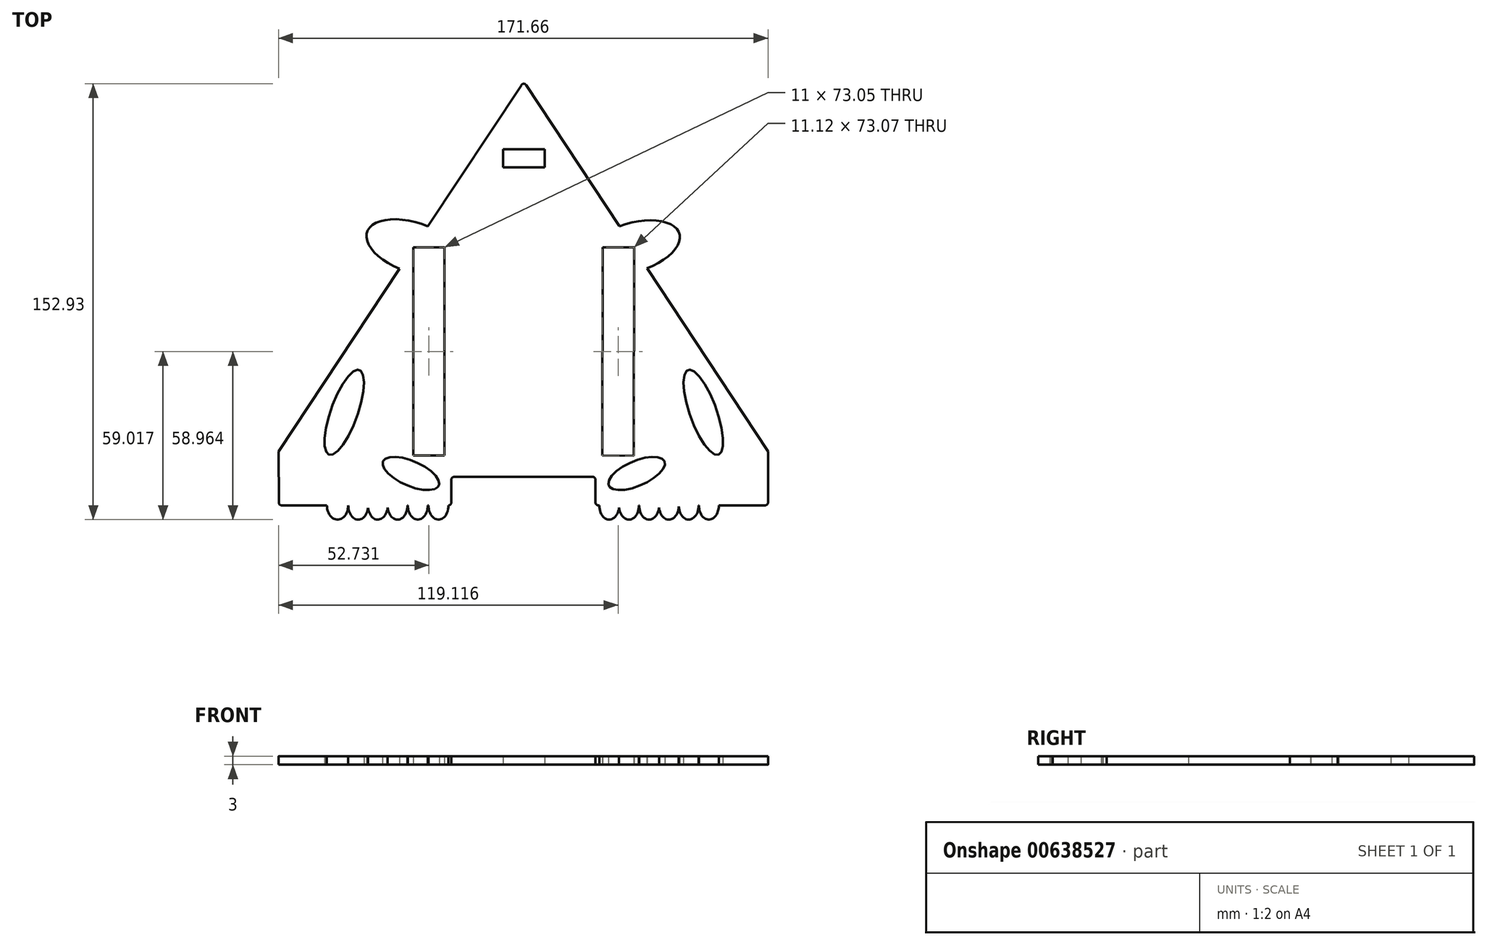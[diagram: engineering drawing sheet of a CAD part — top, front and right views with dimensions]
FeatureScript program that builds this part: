
annotation { "Feature Type Name" : "Feature", "Feature Type Description" : "" }
export const myFeature = defineFeature(function(context is Context, id is Id, definition is map)
    precondition{}
    {
        {
            var Q0;
            Q0=qCreatedBy(makeId("Top.planeOp"),FACE);
            var sketch = newSketch(context, id + "F0", { "sketchPlane" : qUnion([Q0])});
            skPoint(sketch, "E0.0.midPoint", {"position": v(0, -49.5) * mm});
            skPoint(sketch, "E0.cCircle.center.orphan", {"position": v(0, 0) * mm});
            skLineSegment(sketch, "E1", {"start": v(-84.79, -49.5) * mm, "end": v(-54.5, -49.5) * mm});
            skLineSegment(sketch, "E2", {"start": v(84.78, -49.5) * mm, "end": v(26.28, -49.5) * mm});
            skLineSegment(sketch, "E3", {"start": v(25.28, -48.5) * mm, "end": v(25.28, -40.5) * mm});
            skLineSegment(sketch, "E4", {"start": v(24.28, -39.5) * mm, "end": v(-24.28, -39.5) * mm});
            skLineSegment(sketch, "E5", {"start": v(-25.28, -40.5) * mm, "end": v(-25.28, -48.5) * mm});
            skPoint(sketch, "E6.visualSharp", {"position": v(0.12, 99.24) * mm});
            skLineSegment(sketch, "E7", {"start": v(0.95, 97.98) * mm, "end": v(33.62, 48.48) * mm});
            skLineSegment(sketch, "E8", {"start": v(85.78, -30.56) * mm, "end": v(85.78, -48.5) * mm});
            skLineSegment(sketch, "E9", {"start": v(-85.88, -30.62) * mm, "end": v(-85.79, -48.5) * mm});
            skLineSegment(sketch, "E10", {"start": v(-0.72, 97.98) * mm, "end": v(-33.51, 48.46) * mm});
            skArc(sketch, "E11.filletArc", {"start": v(0.95, 97.98) * mm, "mid": v(0.12, 98.43) * mm, "end": v(-0.72, 97.98) * mm});
            skPoint(sketch, "E12.visualSharp", {"position": v(85.78, -49.5) * mm});
            skArc(sketch, "E12.filletArc", {"start": v(84.78, -49.5) * mm, "mid": v(85.49, -49.2) * mm, "end": v(85.78, -48.5) * mm});
            skPoint(sketch, "E13.visualSharp", {"position": v(25.28, -49.5) * mm});
            skArc(sketch, "E13.filletArc", {"start": v(25.28, -48.5) * mm, "mid": v(25.57, -49.2) * mm, "end": v(26.28, -49.5) * mm});
            skPoint(sketch, "E14.visualSharp", {"position": v(-85.78, -49.5) * mm});
            skArc(sketch, "E14.filletArc", {"start": v(-85.79, -48.5) * mm, "mid": v(-85.5, -49.2) * mm, "end": v(-84.79, -49.5) * mm});
            skPoint(sketch, "E15.visualSharp", {"position": v(-25.28, -49.5) * mm});
            skArc(sketch, "E15.filletArc", {"start": v(-26.28, -49.5) * mm, "mid": v(-25.57, -49.2) * mm, "end": v(-25.28, -48.5) * mm});
            skPoint(sketch, "E16.visualSharp", {"position": v(25.28, -39.5) * mm});
            skArc(sketch, "E16.filletArc", {"start": v(25.28, -40.5) * mm, "mid": v(24.99, -39.8) * mm, "end": v(24.28, -39.5) * mm});
            skPoint(sketch, "E17.visualSharp", {"position": v(-25.28, -39.5) * mm});
            skArc(sketch, "E17.filletArc", {"start": v(-24.28, -39.5) * mm, "mid": v(-24.99, -39.8) * mm, "end": v(-25.28, -40.5) * mm});
            skEllipticalArc(sketch, "E18", {});
            skEllipticalArc(sketch, "E19", {});
            skEllipticalArc(sketch, "E20", {});
            skEllipticalArc(sketch, "E21", {});
            skEllipticalArc(sketch, "E22", {});
            skEllipticalArc(sketch, "E23", {});
            skPoint(sketch, "E24", {"position": v(-54.44, -49.5) * mm});
            skPoint(sketch, "E25", {"position": v(-54.56, -49.5) * mm});
            skPoint(sketch, "E26", {"position": v(-54.49, -50.37) * mm});
            skLineSegment(sketch, "E27", {"start": v(-54.5, -49.5) * mm, "end": v(-54.5, -50.43) * mm});
            skPoint(sketch, "E28", {"position": v(-47.57, -49.95) * mm});
            skLineSegment(sketch, "E29", {"start": v(-47.6, -50.28) * mm, "end": v(-47.6, -49.5) * mm});
            skLineSegment(sketch, "E30.trimOffspring", {"start": v(-54.44, -49.5) * mm, "end": v(-26.28, -49.5) * mm});
            skEllipticalArc(sketch, "E31", {});
            skEllipticalArc(sketch, "E32", {});
            skEllipticalArc(sketch, "E33", {});
            skEllipticalArc(sketch, "E34", {});
            skEllipticalArc(sketch, "E35", {});
            skEllipticalArc(sketch, "E36", {});
            skPoint(sketch, "E37", {"position": v(26.6, -49.5) * mm});
            skPoint(sketch, "E38", {"position": v(33.53, -49.5) * mm});
            skPoint(sketch, "E39", {"position": v(40.6, -49.5) * mm});
            skPoint(sketch, "E40", {"position": v(40.53, -49.5) * mm});
            skPoint(sketch, "E41", {"position": v(47.6, -49.5) * mm});
            skPoint(sketch, "E42", {"position": v(47.52, -49.5) * mm});
            skPoint(sketch, "E43", {"position": v(54.52, -49.5) * mm});
            skPoint(sketch, "E44", {"position": v(54.5, -49.5) * mm});
            skPoint(sketch, "E45", {"position": v(61.53, -49.5) * mm});
            skPoint(sketch, "E46", {"position": v(61.5, -49.5) * mm});
            skPoint(sketch, "E47", {"position": v(68.53, -49.5) * mm});
            skPoint(sketch, "E48", {"position": v(33.6, -49.5) * mm});
            skLineSegment(sketch, "E49.trimOffspring", {"start": v(-43.3, 33.68) * mm, "end": v(-85.88, -30.62) * mm});
            skEllipticalArc(sketch, "E50", {});
            skLineSegment(sketch, "E51.trimOffspring", {"start": v(43.37, 33.7) * mm, "end": v(85.78, -30.56) * mm});
            skEllipticalArc(sketch, "E52", {});
            skPoint(sketch, "E53", {"position": v(-33.51, 48.46) * mm});
            skPoint(sketch, "E54", {"position": v(-43.3, 33.68) * mm});
            skLineSegment(sketch, "E55", {"start": v(-33.51, 48.46) * mm, "end": v(-33.56, 48.43) * mm});
            skLineSegment(sketch, "E56", {"start": v(33.62, 48.48) * mm, "end": v(33.68, 48.44) * mm});
            skEllipse(sketch, "E57", {"center": v(63.09, -16.83) * mm, "majorRadius": 15.8 * mm, "minorRadius": 4.7 * mm, "majorAxis": v(0.34, -0.94)});
            skEllipse(sketch, "E58", {"center": v(39.7, -38.3) * mm, "majorRadius": 10.66 * mm, "minorRadius": 4.36 * mm, "majorAxis": v(0.92, 0.4)});
            skEllipse(sketch, "E59.MirrorC", {"center": v(-62.85, -16.83) * mm, "majorRadius": 15.8 * mm, "minorRadius": 4.7 * mm, "majorAxis": v(-0.34, -0.94)});
            skEllipse(sketch, "E60.MirrorC", {"center": v(-39.47, -38.3) * mm, "majorRadius": 10.66 * mm, "minorRadius": 4.36 * mm, "majorAxis": v(-0.92, 0.4)});
            skLineSegment(sketch, "E61.trimOffspring", {"start": v(43.34, 33.7) * mm, "end": v(43.37, 33.7) * mm});
            skPoint(sketch, "E62", {"position": v(47.56, -50.24) * mm});
            skLineSegment(sketch, "E63", {"start": v(47.6, -49.5) * mm, "end": v(47.56, -50.24) * mm});
            skPoint(sketch, "E64", {"position": v(33.57, -50.25) * mm});
            skLineSegment(sketch, "E65", {"start": v(33.6, -49.5) * mm, "end": v(33.57, -50.25) * mm});
            skPoint(sketch, "E66", {"position": v(54.51, -49.91) * mm});
            skLineSegment(sketch, "E67", {"start": v(54.52, -49.5) * mm, "end": v(54.51, -49.91) * mm});
            skLineSegment(sketch, "E68.bottom", {"start": v(-38.65, 41.04) * mm, "end": v(-27.65, 41.04) * mm});
            skLineSegment(sketch, "E68.top", {"start": v(-38.65, -32) * mm, "end": v(-27.65, -32) * mm});
            skLineSegment(sketch, "E68.left", {"start": v(-38.65, 41.04) * mm, "end": v(-38.65, -32) * mm});
            skLineSegment(sketch, "E68.right", {"start": v(-27.65, 41.04) * mm, "end": v(-27.65, -32) * mm});
            skLineSegment(sketch, "E69", {"start": v(0.12, 99.24) * mm, "end": v(0.12, 97.43) * mm});
            skLineSegment(sketch, "E70.MirrorCS", {"start": v(38.8, 40.98) * mm, "end": v(38.68, -32.07) * mm});
            skLineSegment(sketch, "E71.MirrorCS", {"start": v(27.8, 41) * mm, "end": v(27.68, -32.05) * mm});
            skLineSegment(sketch, "E72.MirrorCS", {"start": v(38.8, 40.98) * mm, "end": v(27.8, 41) * mm});
            skLineSegment(sketch, "E73.MirrorCS", {"start": v(38.68, -32.07) * mm, "end": v(27.68, -32.05) * mm});
            skLineSegment(sketch, "E74.trimOffspring", {"start": v(0, -39.5) * mm, "end": v(0, -49.5) * mm});
            skLineSegment(sketch, "E75.bottom", {"start": v(-7.1, 75.4) * mm, "end": v(7.45, 75.4) * mm});
            skLineSegment(sketch, "E75.top", {"start": v(-7.1, 69.1) * mm, "end": v(7.45, 69.1) * mm});
            skLineSegment(sketch, "E75.left", {"start": v(-7.1, 75.4) * mm, "end": v(-7.1, 69.1) * mm});
            skLineSegment(sketch, "E75.right", {"start": v(7.45, 75.4) * mm, "end": v(7.45, 69.1) * mm});
            const initialGuessF0  = {"E18": [-0.029773190751852446, -0.049500003457069536, 0, -1, 0.005, 0.0035, 4.71238898038469, 1.570801617782238], "E19": [-0.03703267885762637, -0.049500003457069536, 0, -1, 0.005, 0.0035, 4.71238898038469, 1.5707963267948966], "E20": [-0.044144015893520766, -0.049500003457069536, 0, -1, 0.005, 0.0035, 4.869765349263817, 1.5707963267948966], "E21": [-0.05105750903492189, -0.0495000034570694, 0, -1, 0.005, 0.0035, 4.899477820012888, 1.4134199579157412], "E22": [-0.05793535813684248, -0.0495000034570694, 0, -1, 0.005, 0.0035, 4.71238898038469, 1.3953355132787328], "E23": [-0.0651826412828583, -0.049500003457069536, 0, -1, 0.005, 0.0037472831460158185, 4.71238898038469, 1.5707963267948966], "E31": [0.030106185004115105, -0.04950000345706941, 0, -1, 0.005, 0.0035, 4.71238898038469, 1.4211992610709008], "E32": [0.037028003484010696, -0.04950000345706941, 0, -1, 0.005, 0.0035, 4.861986046108686, 1.5707963267948966], "E33": [0.044100940227508545, -0.04950000345706941, 0, -1, 0.005, 0.0035, 4.71238898038469, 1.4227047118263165], "E34": [0.05102432146668434, -0.04950000345706941, 0, -1, 0.005, 0.0035, 4.86048059535327, 1.4879021487114794], "E35": [0.05800028517842293, -0.04950000345706941, 0, -1, 0.005, 0.0035, 4.795283158468107, 1.5707963267948966], "E36": [0.06503187119960785, -0.04950000345706941, 0, -1, 0.005, 0.0035, 4.71238898038469, 1.5707963267948966], "E50": [-0.03864901849318095, 0.041044286321482236, 0.9492587766916142, -0.3144960649577991, 0.01704615903539887, 0.00870253430502145, 1.4229541150383596, 4.586177829477201], "E52": [0.03850801645694656, 0.04107041691606262, -0.9600526165022497, -0.2798195374651036, 0.016875, 0.008521082131865629, 1.724333402399982, 4.865276969991962]};
            skSetInitialGuess(sketch, initialGuessF0);
            skSolve(sketch);
        }
        {
            var Q0;
            Q0=makeQuery(id+"F0.imprint","IMPRINT",FACE,{"disambiguationData":[TD([[makeQuery(id+"F0.imprint","IMPRINT",EDGE,{"derivedFrom":sQuery(id+"F0.wireOp",EDGE,"E3")}),-1.0]])]});
            var Q1;
            {var subQ0=sQuery(id+"F0.wireOp",EDGE,"E23");Q1=makeQuery(id+"F0.imprint","IMPRINT",FACE,{"disambiguationData":[TD([[makeQuery(id+"F0.imprint","IMPRINT",EDGE,{"derivedFrom":subQ0}),1.0]])]});}
            var Q2;
            {var subQ0=sQuery(id+"F0.wireOp",EDGE,"E27");Q2=makeQuery(id+"F0.imprint","IMPRINT",FACE,{"disambiguationData":[TD([[makeQuery(id+"F0.imprint","IMPRINT",EDGE,{"derivedFrom":subQ0}),-1.0]])]});}
            var Q3;
            {var subQ0=sQuery(id+"F0.wireOp",EDGE,"E19");Q3=makeQuery(id+"F0.imprint","IMPRINT",FACE,{"disambiguationData":[TD([[makeQuery(id+"F0.imprint","IMPRINT",EDGE,{"derivedFrom":subQ0}),1.0]])]});}
            var Q4;
            {var subQ0=sQuery(id+"F0.wireOp",EDGE,"E20");Q4=makeQuery(id+"F0.imprint","IMPRINT",FACE,{"disambiguationData":[TD([[makeQuery(id+"F0.imprint","IMPRINT",EDGE,{"derivedFrom":subQ0}),1.0]])]});}
            var Q5;
            {var subQ3=sQuery(id+"F0.wireOp",EDGE,"E18");Q5=makeQuery(id+"F0.imprint","IMPRINT",FACE,{"disambiguationData":[TD([[makeQuery(id+"F0.imprint","IMPRINT",EDGE,{"derivedFrom":subQ3}),1.0]])]});}
            var Q6;
            {var subQ0=sQuery(id+"F0.wireOp",EDGE,"E31");Q6=makeQuery(id+"F0.imprint","IMPRINT",FACE,{"disambiguationData":[TD([[makeQuery(id+"F0.imprint","IMPRINT",EDGE,{"derivedFrom":subQ0}),1.0]])]});}
            var Q7;
            Q7=makeQuery(id+"F0.imprint","IMPRINT",FACE,{"disambiguationData":[TD([[makeQuery(id+"F0.imprint","IMPRINT",EDGE,{"derivedFrom":sQuery(id+"F0.wireOp",EDGE,"E34")}),1.0]])]});
            var Q8;
            {var subQ0=sQuery(id+"F0.wireOp",EDGE,"E33");Q8=makeQuery(id+"F0.imprint","IMPRINT",FACE,{"disambiguationData":[TD([[makeQuery(id+"F0.imprint","IMPRINT",EDGE,{"derivedFrom":subQ0}),1.0]])]});}
            var Q9;
            {var subQ0=sQuery(id+"F0.wireOp",EDGE,"E32");Q9=makeQuery(id+"F0.imprint","IMPRINT",FACE,{"disambiguationData":[TD([[makeQuery(id+"F0.imprint","IMPRINT",EDGE,{"derivedFrom":subQ0}),1.0]])]});}
            var Q10;
            {var subQ0=sQuery(id+"F0.wireOp",EDGE,"E35");Q10=makeQuery(id+"F0.imprint","IMPRINT",FACE,{"disambiguationData":[TD([[makeQuery(id+"F0.imprint","IMPRINT",EDGE,{"derivedFrom":subQ0}),1.0]])]});}
            var Q11;
            {var subQ0=sQuery(id+"F0.wireOp",EDGE,"E36");Q11=makeQuery(id+"F0.imprint","IMPRINT",FACE,{"disambiguationData":[TD([[makeQuery(id+"F0.imprint","IMPRINT",EDGE,{"derivedFrom":subQ0}),1.0]])]});}
            extrude(context, id + "F1", {"entities" : qUnion([Q0, Q1, Q2, Q3, Q4, Q5, Q6, Q7, Q8, Q9, Q10, Q11]), "depth" : 3 * mm, "offsetDistance" : 25 * mm});
        }
    });
